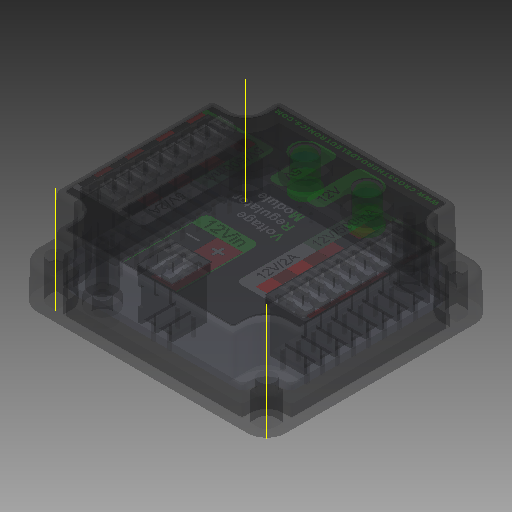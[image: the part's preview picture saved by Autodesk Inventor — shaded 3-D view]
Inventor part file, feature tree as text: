
AUTODESK INVENTOR PART (.ipt)
format: ipt  version: 2019 (Build 230136000, 136)  size: 6,934,528 bytes
history: native  units: in
note: dims shown in document units (in); Inventor stores cm internally (conversion verified against a paired STEP export)
features: other x6, plane x2, sketch x1
ambient origin geometry x8: Origin, YZ Plane, XZ Plane, XY Plane, X Axis, Y Axis, Z Axis, Center Point
bodies: Body1 (feature_tree), Body2 (feature_tree), Body3 (feature_tree), Body4 (feature_tree), Body5 (feature_tree), Body6 (feature_tree), Body7 (feature_tree), Body8 (feature_tree), Body9 (feature_tree), Body10 (feature_tree), Body11 (feature_tree), Body12 (feature_tree), Body13 (feature_tree), Body14 (feature_tree), Body15 (feature_tree), Body16 (feature_tree), Body17 (feature_tree), Body18 (feature_tree), Body19 (feature_tree), Body20 (feature_tree), Body21 (feature_tree), Body22 (feature_tree), Body23 (feature_tree), Body24 (feature_tree), Body25 (feature_tree), Body26 (feature_tree), Body27 (feature_tree), Body28 (feature_tree), Body29 (feature_tree), Body30 (feature_tree), Body31 (feature_tree), Body32 (feature_tree), Body33 (feature_tree), Body34 (feature_tree)
feature tree (9):
  other  "vrm1"
  other  "Work Axis2"
  plane  "Work Plane1"
  plane  "Work Plane2"
  sketch  "Sketch1"  dims[d0=1.695in d1=1.8799in]
  other  "Work Axis1"
  other  "Work Axis3"
  other  "Composite1"
  other  "Srf1"
